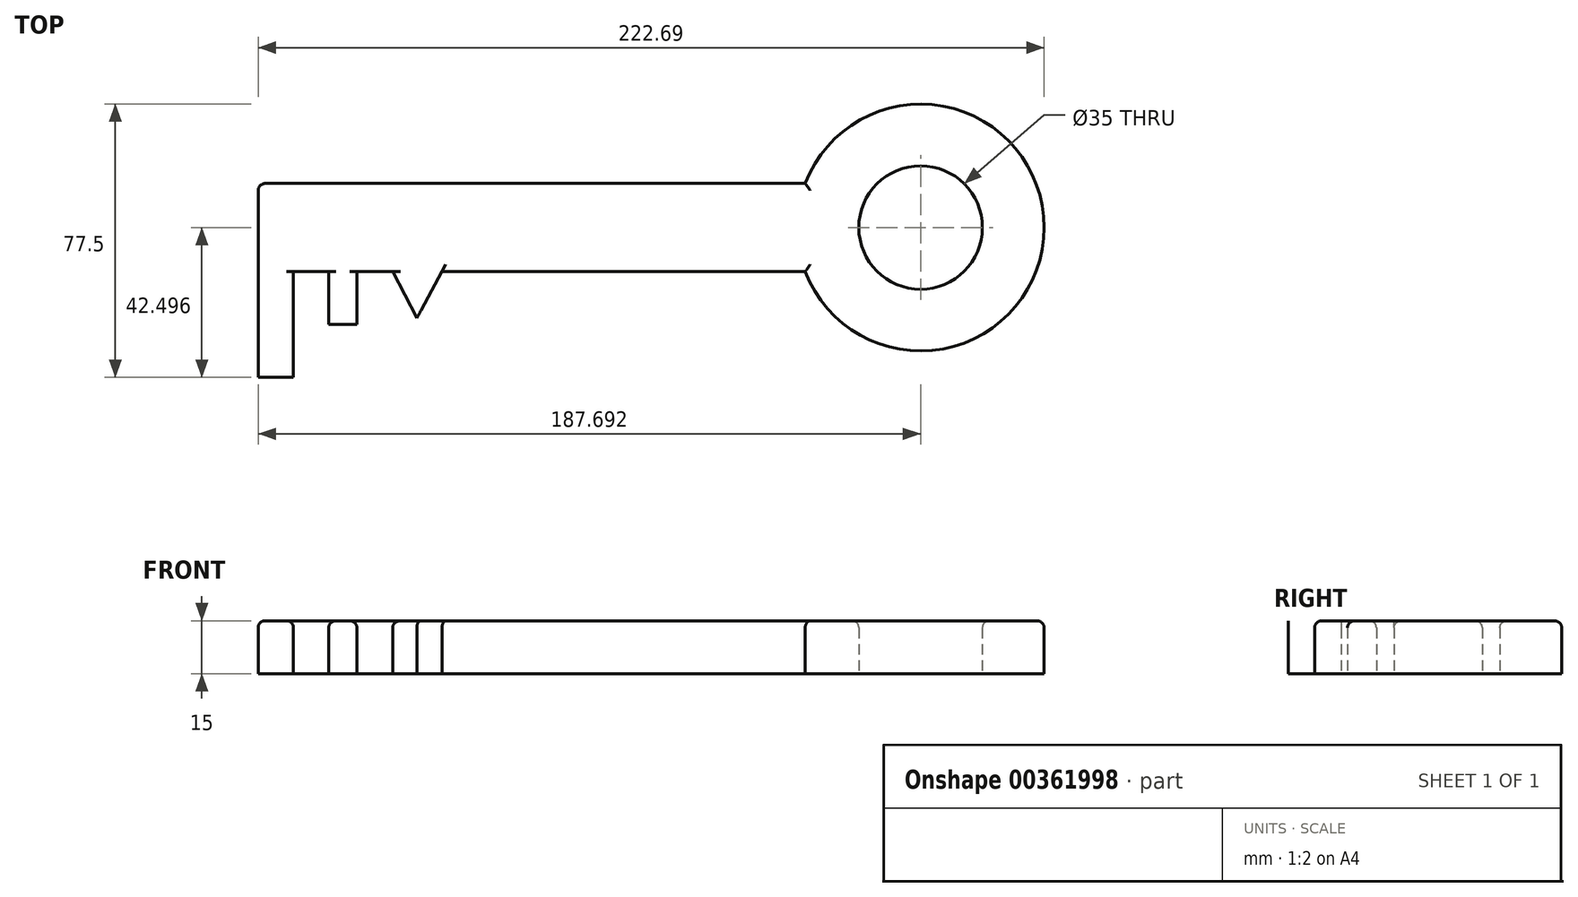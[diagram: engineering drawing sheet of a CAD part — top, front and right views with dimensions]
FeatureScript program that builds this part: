
annotation { "Feature Type Name" : "Feature", "Feature Type Description" : "" }
export const myFeature = defineFeature(function(context is Context, id is Id, definition is map)
    precondition{}
    {
        {
            var Q0;
            Q0=qCreatedBy(makeId("Top.planeOp"),FACE);
            var sketch = newSketch(context, id + "F0", { "sketchPlane" : qUnion([Q0])});
            skLineSegment(sketch, "E0.bottom", {"start": v(-155, 16.05) * mm, "end": v(0, 16.05) * mm});
            skLineSegment(sketch, "E0.top", {"start": v(-155, -8.95) * mm, "end": v(0, -8.95) * mm});
            skLineSegment(sketch, "E0.left", {"start": v(-155, 16.05) * mm, "end": v(-155, -8.95) * mm});
            skLineSegment(sketch, "E0.right", {"start": v(0, 16.05) * mm, "end": v(0, -8.95) * mm});
            skLineSegment(sketch, "E1.bottom", {"start": v(-155, -8.95) * mm, "end": v(-145, -8.95) * mm});
            skLineSegment(sketch, "E1.top", {"start": v(-155, -38.95) * mm, "end": v(-145, -38.95) * mm});
            skLineSegment(sketch, "E1.left", {"start": v(-155, -8.95) * mm, "end": v(-155, -38.95) * mm});
            skLineSegment(sketch, "E1.right", {"start": v(-145, -8.95) * mm, "end": v(-145, -38.95) * mm});
            skLineSegment(sketch, "E2.bottom", {"start": v(-135.04, -8.95) * mm, "end": v(-127.04, -8.95) * mm});
            skLineSegment(sketch, "E2.top", {"start": v(-135.04, -23.95) * mm, "end": v(-127.04, -23.95) * mm});
            skLineSegment(sketch, "E2.left", {"start": v(-135.04, -8.95) * mm, "end": v(-135.04, -23.95) * mm});
            skLineSegment(sketch, "E2.right", {"start": v(-127.04, -8.95) * mm, "end": v(-127.04, -23.95) * mm});
            skLineSegment(sketch, "E3", {"start": v(-116.91, -8.95) * mm, "end": v(-110.05, -22.14) * mm});
            skLineSegment(sketch, "E4", {"start": v(-110.05, -22.14) * mm, "end": v(-102.91, -8.95) * mm});
            skArc(sketch, "E5", {"start": v(0, -8.95) * mm, "mid": v(67.7, 3.55) * mm, "end": v(0, 16.05) * mm});
            skCircle(sketch, "E6", {"center": v(32.7, 3.55) * mm, "radius": 17.5 * mm});
            skSolve(sketch);
        }
        {
            var Q0;
            Q0 = qSketchRegion(id + "F0", true);
            extrude(context, id + "F1", {"entities" : qUnion([Q0]), "depth" : 15 * mm});
        }
        {
            var Q0;
            Q0=makeQuery(id+"F1.opExtrude","CAP_EDGE",EDGE,{"disambiguationData":[OSD([sQuery(id+"F0.wireOp",EDGE,"E0.bottom")])],"isStart":false});
            fillet(context, id + "F2", {"entities" : qUnion([Q0]), "radius" : 2 * mm, "tangentPropagation" : true, "allowEdgeOverflow" : false});
        }
        {
            var Q0;
            Q0=makeQuery(id+"F1.opExtrude","CAP_EDGE",EDGE,{"disambiguationData":[OSD([sQuery(id+"F0.wireOp",EDGE,"E0.left"),sQuery(id+"F0.wireOp",EDGE,"E1.left")])],"isStart":false});
            fillet(context, id + "F3", {"entities" : qUnion([Q0]), "radius" : 2 * mm, "tangentPropagation" : true, "allowEdgeOverflow" : false});
        }
        {
            var Q0;
            Q0=makeQuery(id+"F1.opExtrude","CAP_EDGE",EDGE,{"disambiguationData":[OSD([sQuery(id+"F0.wireOp",EDGE,"E1.right")])],"isStart":false});
            fillet(context, id + "F4", {"entities" : qUnion([Q0]), "radius" : 2 * mm, "tangentPropagation" : true, "allowEdgeOverflow" : false});
        }
        {
            var Q0;
            Q0=makeQuery(id+"F1.opExtrude","CAP_EDGE",EDGE,{"disambiguationData":[OSD([sQuery(id+"F0.wireOp",EDGE,"E2.left")])],"isStart":false});
            fillet(context, id + "F5", {"entities" : qUnion([Q0]), "radius" : 2 * mm, "tangentPropagation" : true, "allowEdgeOverflow" : false});
        }
        {
            var Q0;
            Q0=makeQuery(id+"F1.opExtrude","CAP_EDGE",EDGE,{"disambiguationData":[OSD([sQuery(id+"F0.wireOp",EDGE,"E2.right")])],"isStart":false});
            fillet(context, id + "F6", {"entities" : qUnion([Q0]), "radius" : 2 * mm, "tangentPropagation" : true, "allowEdgeOverflow" : false});
        }
        {
            var Q0;
            Q0=makeQuery(id+"F1.opExtrude","CAP_EDGE",EDGE,{"disambiguationData":[OSD([sQuery(id+"F0.wireOp",EDGE,"E3")])],"isStart":false});
            fillet(context, id + "F7", {"entities" : qUnion([Q0]), "radius" : 2 * mm, "tangentPropagation" : true, "allowEdgeOverflow" : false});
        }
        {
            var Q0;
            {var subQ0=sQuery(id+"F0.wireOp",EDGE,"E0.top");Q0=makeQuery(id+"F1.opExtrude","CAP_EDGE",EDGE,{"disambiguationData":[OSD([subQ0]),TDD([makeQuery(id+"F0.imprint","IMPRINT",EDGE,{"disambiguationData":[TD([[makeQuery(id+"F0.imprint","INTERSECT",VERTEX,{"derivedFrom":[subQ0,sQuery(id+"F0.wireOp",EDGE,"E4")]}),-1.0]])],"derivedFrom":subQ0})])],"isStart":false});}
            fillet(context, id + "F8", {"entities" : qUnion([Q0]), "radius" : 2 * mm, "tangentPropagation" : true, "allowEdgeOverflow" : false});
        }
        {
            var Q0;
            Q0=makeQuery(id+"F1.opExtrude","CAP_EDGE",EDGE,{"disambiguationData":[OSD([sQuery(id+"F0.wireOp",EDGE,"E5")])],"isStart":false});
            fillet(context, id + "F9", {"entities" : qUnion([Q0]), "radius" : 2 * mm, "tangentPropagation" : true, "allowEdgeOverflow" : false});
        }
        {
            var Q0;
            Q0=makeQuery(id+"F1.opExtrude","CAP_EDGE",EDGE,{"disambiguationData":[OSD([sQuery(id+"F0.wireOp",EDGE,"E6")])],"isStart":false});
            fillet(context, id + "F10", {"entities" : qUnion([Q0]), "radius" : 2 * mm, "tangentPropagation" : true, "allowEdgeOverflow" : false});
        }
    });
